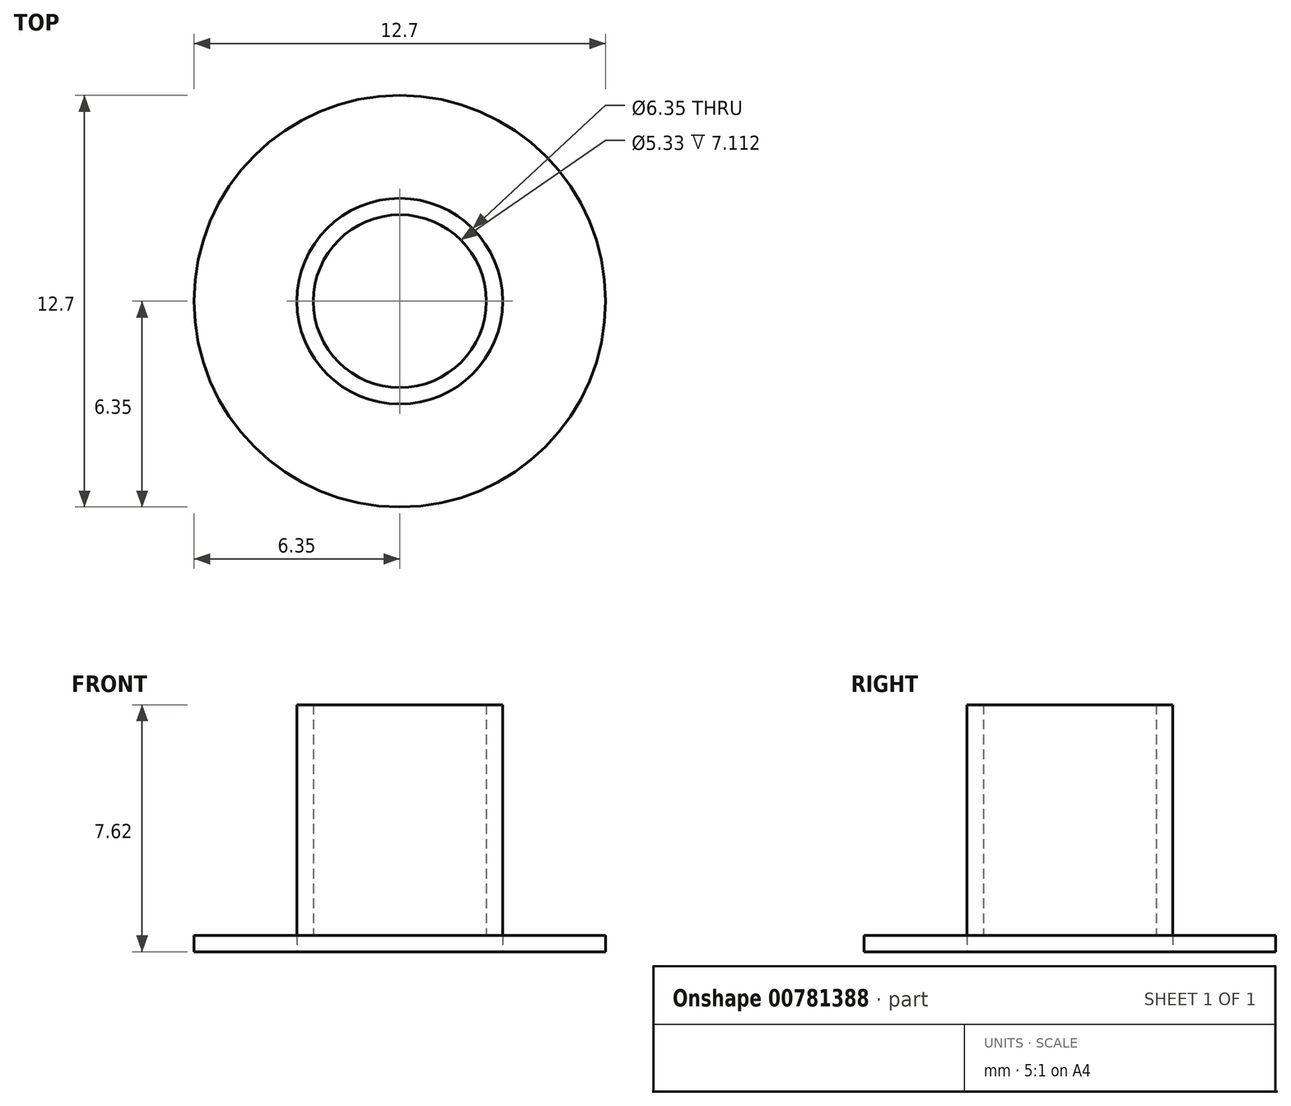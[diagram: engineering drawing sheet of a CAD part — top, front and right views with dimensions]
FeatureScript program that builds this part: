
annotation { "Feature Type Name" : "Feature", "Feature Type Description" : "" }
export const myFeature = defineFeature(function(context is Context, id is Id, definition is map)
    precondition{}
    {
        {
            var Q0;
            Q0=qCreatedBy(makeId("Top.planeOp"),FACE);
            var sketch = newSketch(context, id + "F0", { "sketchPlane" : qUnion([Q0])});
            skCircle(sketch, "E0", {"center": v(0, 0) * mm, "radius": 6.35 * mm});
            skCircle(sketch, "E1", {"center": v(0, 0) * mm, "radius": 3.18 * mm});
            skSolve(sketch);
        }
        {
            var Q0;
            Q0=makeQuery(id+"F0.imprint","IMPRINT",FACE,{"disambiguationData":[TD([[makeQuery(id+"F0.imprint","IMPRINT",EDGE,{"derivedFrom":sQuery(id+"F0.wireOp",EDGE,"E1")}),1.0]])]});
            extrude(context, id + "F1", {"entities" : qUnion([Q0]), "depth" : 7.62 * mm, "offsetDistance" : 25.4 * mm});
        }
        {
            var Q0;
            Q0=makeQuery(id+"F1.opExtrude","CAP_FACE",FACE,{"disambiguationData":[OSD([sQuery(id+"F0.wireOp",EDGE,"E1")])],"isStart":false});
            shell(context, id + "F2", {"entities" : qUnion([Q0]), "thickness" : 0.5 * mm});
        }
        {
            var Q0;
            Q0 = qSketchRegion(id + "F0", true);
            extrude(context, id + "F3", {"entities" : qUnion([Q0]), "depth" : 0.5 * mm, "offsetDistance" : 25.4 * mm});
        }
    });
